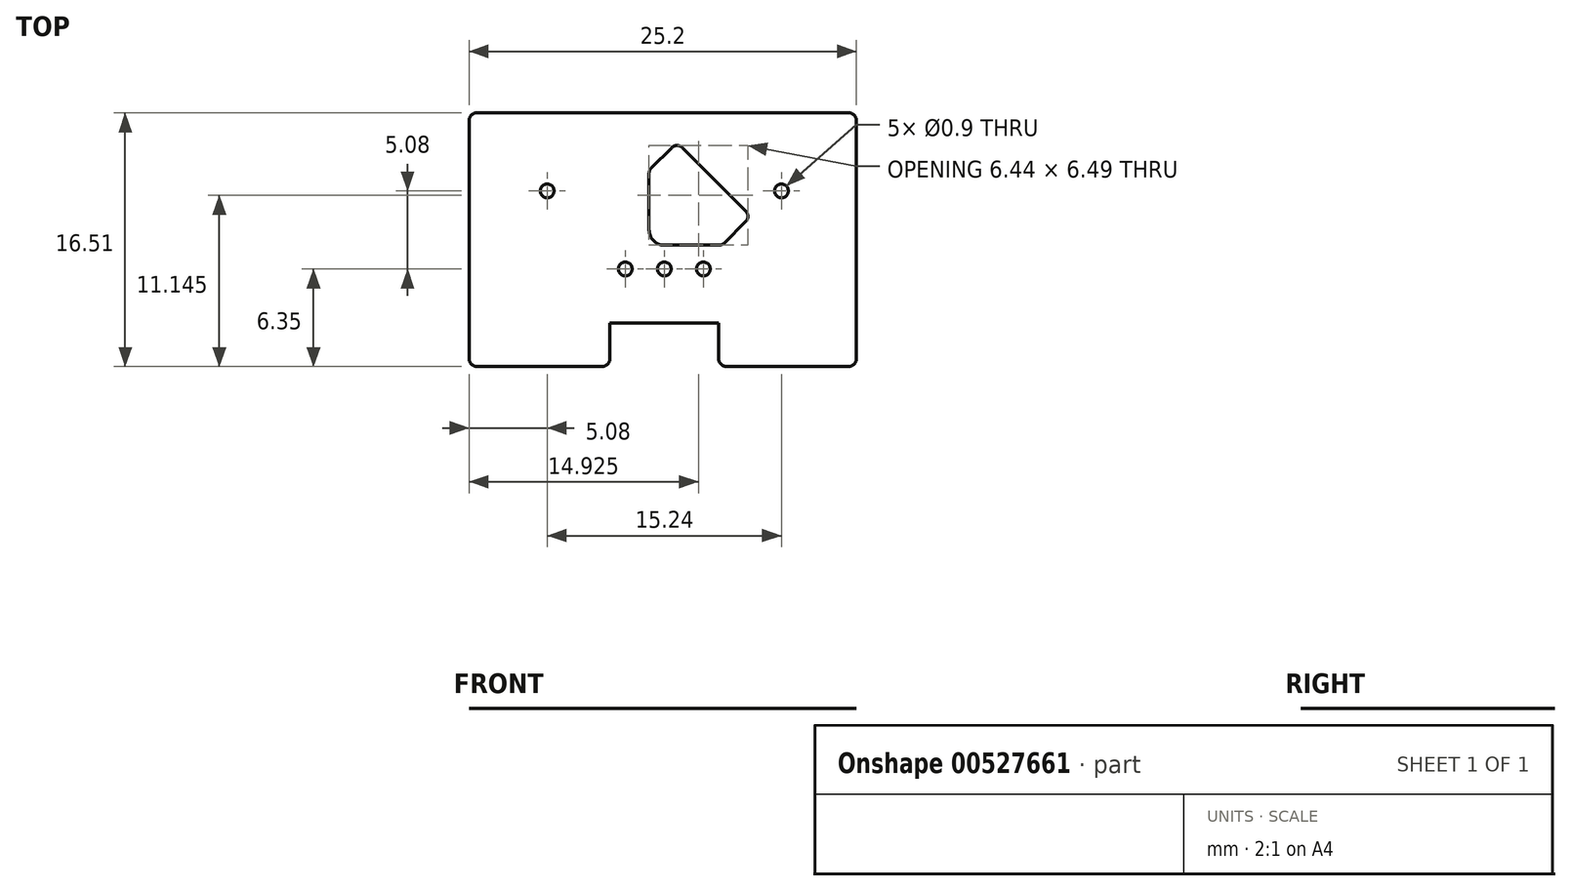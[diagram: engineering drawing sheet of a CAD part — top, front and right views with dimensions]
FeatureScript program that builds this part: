
annotation { "Feature Type Name" : "Feature", "Feature Type Description" : "" }
export const myFeature = defineFeature(function(context is Context, id is Id, definition is map)
    precondition{}
    {
        {
            var Q0;
            Q0=qCreatedBy(makeId("Top.planeOp"),FACE);
            var sketch = newSketch(context, id + "F0", { "sketchPlane" : qUnion([Q0])});
            skCircle(sketch, "E0", {"center": v(0, 0) * mm, "radius": 1 * mm});
            skPoint(sketch, "E1.0.1.0", {"position": v(0, 2.54) * mm});
            skCircle(sketch, "E1.0.1.1", {"center": v(0, 2.54) * mm, "radius": 1 * mm});
            skPoint(sketch, "E1.0.2.0", {"position": v(0, 5.08) * mm});
            skCircle(sketch, "E1.0.2.1", {"center": v(0, 5.08) * mm, "radius": 1 * mm});
            skPoint(sketch, "E1.0.3.0", {"position": v(0, 7.62) * mm});
            skCircle(sketch, "E1.0.3.1", {"center": v(0, 7.62) * mm, "radius": 1 * mm});
            skPoint(sketch, "E1.0.4.0", {"position": v(0, 10.16) * mm});
            skCircle(sketch, "E1.0.4.1", {"center": v(0, 10.16) * mm, "radius": 1 * mm});
            skPoint(sketch, "E1.0.5.0", {"position": v(0, 12.7) * mm});
            skCircle(sketch, "E1.0.5.1", {"center": v(0, 12.7) * mm, "radius": 1 * mm});
            skPoint(sketch, "E1.1.0.0", {"position": v(2.54, 0) * mm});
            skCircle(sketch, "E1.1.0.1", {"center": v(2.54, 0) * mm, "radius": 1 * mm});
            skPoint(sketch, "E1.1.1.0", {"position": v(2.54, 2.54) * mm});
            skCircle(sketch, "E1.1.1.1", {"center": v(2.54, 2.54) * mm, "radius": 1 * mm});
            skPoint(sketch, "E1.1.2.0", {"position": v(2.54, 5.08) * mm});
            skCircle(sketch, "E1.1.2.1", {"center": v(2.54, 5.08) * mm, "radius": 1 * mm});
            skPoint(sketch, "E1.1.3.0", {"position": v(2.54, 7.62) * mm});
            skCircle(sketch, "E1.1.3.1", {"center": v(2.54, 7.62) * mm, "radius": 1 * mm});
            skPoint(sketch, "E1.1.4.0", {"position": v(2.54, 10.16) * mm});
            skCircle(sketch, "E1.1.4.1", {"center": v(2.54, 10.16) * mm, "radius": 1 * mm});
            skPoint(sketch, "E1.1.5.0", {"position": v(2.54, 12.7) * mm});
            skCircle(sketch, "E1.1.5.1", {"center": v(2.54, 12.7) * mm, "radius": 1 * mm});
            skPoint(sketch, "E1.2.0.0", {"position": v(5.08, 0) * mm});
            skCircle(sketch, "E1.2.0.1", {"center": v(5.08, 0) * mm, "radius": 1 * mm});
            skPoint(sketch, "E1.2.1.0", {"position": v(5.08, 2.54) * mm});
            skCircle(sketch, "E1.2.1.1", {"center": v(5.08, 2.54) * mm, "radius": 1 * mm});
            skPoint(sketch, "E1.2.2.0", {"position": v(5.08, 5.08) * mm});
            skCircle(sketch, "E1.2.2.1", {"center": v(5.08, 5.08) * mm, "radius": 1 * mm});
            skPoint(sketch, "E1.2.3.0", {"position": v(5.08, 7.62) * mm});
            skCircle(sketch, "E1.2.3.1", {"center": v(5.08, 7.62) * mm, "radius": 1 * mm});
            skPoint(sketch, "E1.2.4.0", {"position": v(5.08, 10.16) * mm});
            skCircle(sketch, "E1.2.4.1", {"center": v(5.08, 10.16) * mm, "radius": 1 * mm});
            skPoint(sketch, "E1.2.5.0", {"position": v(5.08, 12.7) * mm});
            skCircle(sketch, "E1.2.5.1", {"center": v(5.08, 12.7) * mm, "radius": 1 * mm});
            skPoint(sketch, "E1.3.0.0", {"position": v(7.62, 0) * mm});
            skCircle(sketch, "E1.3.0.1", {"center": v(7.62, 0) * mm, "radius": 1 * mm});
            skPoint(sketch, "E1.3.1.0", {"position": v(7.62, 2.54) * mm});
            skCircle(sketch, "E1.3.1.1", {"center": v(7.62, 2.54) * mm, "radius": 1 * mm});
            skPoint(sketch, "E1.3.2.0", {"position": v(7.62, 5.08) * mm});
            skCircle(sketch, "E1.3.2.1", {"center": v(7.62, 5.08) * mm, "radius": 1 * mm});
            skPoint(sketch, "E1.3.3.0", {"position": v(7.62, 7.62) * mm});
            skCircle(sketch, "E1.3.3.1", {"center": v(7.62, 7.62) * mm, "radius": 1 * mm});
            skPoint(sketch, "E1.3.4.0", {"position": v(7.62, 10.16) * mm});
            skCircle(sketch, "E1.3.4.1", {"center": v(7.62, 10.16) * mm, "radius": 1 * mm});
            skPoint(sketch, "E1.3.5.0", {"position": v(7.62, 12.7) * mm});
            skCircle(sketch, "E1.3.5.1", {"center": v(7.62, 12.7) * mm, "radius": 1 * mm});
            skPoint(sketch, "E1.4.0.0", {"position": v(10.16, 0) * mm});
            skCircle(sketch, "E1.4.0.1", {"center": v(10.16, 0) * mm, "radius": 1 * mm});
            skPoint(sketch, "E1.4.1.0", {"position": v(10.16, 2.54) * mm});
            skCircle(sketch, "E1.4.1.1", {"center": v(10.16, 2.54) * mm, "radius": 1 * mm});
            skPoint(sketch, "E1.4.2.0", {"position": v(10.16, 5.08) * mm});
            skCircle(sketch, "E1.4.2.1", {"center": v(10.16, 5.08) * mm, "radius": 1 * mm});
            skPoint(sketch, "E1.4.3.0", {"position": v(10.16, 7.62) * mm});
            skCircle(sketch, "E1.4.3.1", {"center": v(10.16, 7.62) * mm, "radius": 1 * mm});
            skPoint(sketch, "E1.4.4.0", {"position": v(10.16, 10.16) * mm});
            skCircle(sketch, "E1.4.4.1", {"center": v(10.16, 10.16) * mm, "radius": 1 * mm});
            skPoint(sketch, "E1.4.5.0", {"position": v(10.16, 12.7) * mm});
            skCircle(sketch, "E1.4.5.1", {"center": v(10.16, 12.7) * mm, "radius": 1 * mm});
            skPoint(sketch, "E1.5.0.0", {"position": v(12.7, 0) * mm});
            skCircle(sketch, "E1.5.0.1", {"center": v(12.7, 0) * mm, "radius": 1 * mm});
            skPoint(sketch, "E1.5.1.0", {"position": v(12.7, 2.54) * mm});
            skCircle(sketch, "E1.5.1.1", {"center": v(12.7, 2.54) * mm, "radius": 1 * mm});
            skPoint(sketch, "E1.5.2.0", {"position": v(12.7, 5.08) * mm});
            skCircle(sketch, "E1.5.2.1", {"center": v(12.7, 5.08) * mm, "radius": 1 * mm});
            skPoint(sketch, "E1.5.3.0", {"position": v(12.7, 7.62) * mm});
            skCircle(sketch, "E1.5.3.1", {"center": v(12.7, 7.62) * mm, "radius": 1 * mm});
            skPoint(sketch, "E1.5.4.0", {"position": v(12.7, 10.16) * mm});
            skCircle(sketch, "E1.5.4.1", {"center": v(12.7, 10.16) * mm, "radius": 1 * mm});
            skPoint(sketch, "E1.5.5.0", {"position": v(12.7, 12.7) * mm});
            skCircle(sketch, "E1.5.5.1", {"center": v(12.7, 12.7) * mm, "radius": 1 * mm});
            skPoint(sketch, "E1.6.0.0", {"position": v(15.24, 0) * mm});
            skCircle(sketch, "E1.6.0.1", {"center": v(15.24, 0) * mm, "radius": 1 * mm});
            skPoint(sketch, "E1.6.1.0", {"position": v(15.24, 2.54) * mm});
            skCircle(sketch, "E1.6.1.1", {"center": v(15.24, 2.54) * mm, "radius": 1 * mm});
            skPoint(sketch, "E1.6.2.0", {"position": v(15.24, 5.08) * mm});
            skCircle(sketch, "E1.6.2.1", {"center": v(15.24, 5.08) * mm, "radius": 1 * mm});
            skPoint(sketch, "E1.6.3.0", {"position": v(15.24, 7.62) * mm});
            skCircle(sketch, "E1.6.3.1", {"center": v(15.24, 7.62) * mm, "radius": 1 * mm});
            skPoint(sketch, "E1.6.4.0", {"position": v(15.24, 10.16) * mm});
            skCircle(sketch, "E1.6.4.1", {"center": v(15.24, 10.16) * mm, "radius": 1 * mm});
            skPoint(sketch, "E1.6.5.0", {"position": v(15.24, 12.7) * mm});
            skCircle(sketch, "E1.6.5.1", {"center": v(15.24, 12.7) * mm, "radius": 1 * mm});
            skPoint(sketch, "E1.7.0.0", {"position": v(17.78, 0) * mm});
            skCircle(sketch, "E1.7.0.1", {"center": v(17.78, 0) * mm, "radius": 1 * mm});
            skPoint(sketch, "E1.7.1.0", {"position": v(17.78, 2.54) * mm});
            skCircle(sketch, "E1.7.1.1", {"center": v(17.78, 2.54) * mm, "radius": 1 * mm});
            skPoint(sketch, "E1.7.2.0", {"position": v(17.78, 5.08) * mm});
            skCircle(sketch, "E1.7.2.1", {"center": v(17.78, 5.08) * mm, "radius": 1 * mm});
            skPoint(sketch, "E1.7.3.0", {"position": v(17.78, 7.62) * mm});
            skCircle(sketch, "E1.7.3.1", {"center": v(17.78, 7.62) * mm, "radius": 1 * mm});
            skPoint(sketch, "E1.7.4.0", {"position": v(17.78, 10.16) * mm});
            skCircle(sketch, "E1.7.4.1", {"center": v(17.78, 10.16) * mm, "radius": 1 * mm});
            skPoint(sketch, "E1.7.5.0", {"position": v(17.78, 12.7) * mm});
            skCircle(sketch, "E1.7.5.1", {"center": v(17.78, 12.7) * mm, "radius": 1 * mm});
            skLineSegment(sketch, "E1.direction1", {"start": v(0, 0) * mm, "end": v(2.54, 0) * mm, "construction": true});
            skLineSegment(sketch, "E1.direction2", {"start": v(0, 0) * mm, "end": v(0, 2.54) * mm, "construction": true});
            skPoint(sketch, "E2.0.0.6", {"position": v(0, 15.24) * mm});
            skCircle(sketch, "E2.1.0.6", {"center": v(0, 15.24) * mm, "radius": 1 * mm});
            skPoint(sketch, "E2.0.0.7", {"position": v(0, 17.78) * mm});
            skCircle(sketch, "E2.1.0.7", {"center": v(0, 17.78) * mm, "radius": 1 * mm});
            skPoint(sketch, "E2.0.1.6", {"position": v(2.54, 15.24) * mm});
            skCircle(sketch, "E2.1.1.6", {"center": v(2.54, 15.24) * mm, "radius": 1 * mm});
            skPoint(sketch, "E2.0.1.7", {"position": v(2.54, 17.78) * mm});
            skCircle(sketch, "E2.1.1.7", {"center": v(2.54, 17.78) * mm, "radius": 1 * mm});
            skPoint(sketch, "E2.0.2.6", {"position": v(5.08, 15.24) * mm});
            skCircle(sketch, "E2.1.2.6", {"center": v(5.08, 15.24) * mm, "radius": 1 * mm});
            skPoint(sketch, "E2.0.2.7", {"position": v(5.08, 17.78) * mm});
            skCircle(sketch, "E2.1.2.7", {"center": v(5.08, 17.78) * mm, "radius": 1 * mm});
            skPoint(sketch, "E2.0.3.6", {"position": v(7.62, 15.24) * mm});
            skCircle(sketch, "E2.1.3.6", {"center": v(7.62, 15.24) * mm, "radius": 1 * mm});
            skPoint(sketch, "E2.0.3.7", {"position": v(7.62, 17.78) * mm});
            skCircle(sketch, "E2.1.3.7", {"center": v(7.62, 17.78) * mm, "radius": 1 * mm});
            skPoint(sketch, "E2.0.4.6", {"position": v(10.16, 15.24) * mm});
            skCircle(sketch, "E2.1.4.6", {"center": v(10.16, 15.24) * mm, "radius": 1 * mm});
            skPoint(sketch, "E2.0.4.7", {"position": v(10.16, 17.78) * mm});
            skCircle(sketch, "E2.1.4.7", {"center": v(10.16, 17.78) * mm, "radius": 1 * mm});
            skPoint(sketch, "E2.0.5.6", {"position": v(12.7, 15.24) * mm});
            skCircle(sketch, "E2.1.5.6", {"center": v(12.7, 15.24) * mm, "radius": 1 * mm});
            skPoint(sketch, "E2.0.5.7", {"position": v(12.7, 17.78) * mm});
            skCircle(sketch, "E2.1.5.7", {"center": v(12.7, 17.78) * mm, "radius": 1 * mm});
            skPoint(sketch, "E2.0.6.6", {"position": v(15.24, 15.24) * mm});
            skCircle(sketch, "E2.1.6.6", {"center": v(15.24, 15.24) * mm, "radius": 1 * mm});
            skPoint(sketch, "E2.0.6.7", {"position": v(15.24, 17.78) * mm});
            skCircle(sketch, "E2.1.6.7", {"center": v(15.24, 17.78) * mm, "radius": 1 * mm});
            skPoint(sketch, "E2.0.7.6", {"position": v(17.78, 15.24) * mm});
            skCircle(sketch, "E2.1.7.6", {"center": v(17.78, 15.24) * mm, "radius": 1 * mm});
            skPoint(sketch, "E2.0.7.7", {"position": v(17.78, 17.78) * mm});
            skCircle(sketch, "E2.1.7.7", {"center": v(17.78, 17.78) * mm, "radius": 1 * mm});
            skPoint(sketch, "E3.0.8.0", {"position": v(20.32, 0) * mm});
            skCircle(sketch, "E3.1.8.0", {"center": v(20.32, 0) * mm, "radius": 1 * mm});
            skPoint(sketch, "E3.0.8.1", {"position": v(20.32, 2.54) * mm});
            skCircle(sketch, "E3.1.8.1", {"center": v(20.32, 2.54) * mm, "radius": 1 * mm});
            skPoint(sketch, "E3.0.8.2", {"position": v(20.32, 5.08) * mm});
            skCircle(sketch, "E3.1.8.2", {"center": v(20.32, 5.08) * mm, "radius": 1 * mm});
            skPoint(sketch, "E3.0.8.3", {"position": v(20.32, 7.62) * mm});
            skCircle(sketch, "E3.1.8.3", {"center": v(20.32, 7.62) * mm, "radius": 1 * mm});
            skPoint(sketch, "E3.0.8.4", {"position": v(20.32, 10.16) * mm});
            skCircle(sketch, "E3.1.8.4", {"center": v(20.32, 10.16) * mm, "radius": 1 * mm});
            skPoint(sketch, "E3.0.8.5", {"position": v(20.32, 12.7) * mm});
            skCircle(sketch, "E3.1.8.5", {"center": v(20.32, 12.7) * mm, "radius": 1 * mm});
            skPoint(sketch, "E3.0.8.6", {"position": v(20.32, 15.24) * mm});
            skCircle(sketch, "E3.1.8.6", {"center": v(20.32, 15.24) * mm, "radius": 1 * mm});
            skPoint(sketch, "E3.0.8.7", {"position": v(20.32, 17.78) * mm});
            skCircle(sketch, "E3.1.8.7", {"center": v(20.32, 17.78) * mm, "radius": 1 * mm});
            skPoint(sketch, "E3.0.9.0", {"position": v(22.86, 0) * mm});
            skCircle(sketch, "E3.1.9.0", {"center": v(22.86, 0) * mm, "radius": 1 * mm});
            skPoint(sketch, "E3.0.9.1", {"position": v(22.86, 2.54) * mm});
            skCircle(sketch, "E3.1.9.1", {"center": v(22.86, 2.54) * mm, "radius": 1 * mm});
            skPoint(sketch, "E3.0.9.2", {"position": v(22.86, 5.08) * mm});
            skCircle(sketch, "E3.1.9.2", {"center": v(22.86, 5.08) * mm, "radius": 1 * mm});
            skPoint(sketch, "E3.0.9.3", {"position": v(22.86, 7.62) * mm});
            skCircle(sketch, "E3.1.9.3", {"center": v(22.86, 7.62) * mm, "radius": 1 * mm});
            skPoint(sketch, "E3.0.9.4", {"position": v(22.86, 10.16) * mm});
            skCircle(sketch, "E3.1.9.4", {"center": v(22.86, 10.16) * mm, "radius": 1 * mm});
            skPoint(sketch, "E3.0.9.5", {"position": v(22.86, 12.7) * mm});
            skCircle(sketch, "E3.1.9.5", {"center": v(22.86, 12.7) * mm, "radius": 1 * mm});
            skPoint(sketch, "E3.0.9.6", {"position": v(22.86, 15.24) * mm});
            skCircle(sketch, "E3.1.9.6", {"center": v(22.86, 15.24) * mm, "radius": 1 * mm});
            skPoint(sketch, "E3.0.9.7", {"position": v(22.86, 17.78) * mm});
            skCircle(sketch, "E3.1.9.7", {"center": v(22.86, 17.78) * mm, "radius": 1 * mm});
            skPoint(sketch, "E3.0.10.0", {"position": v(25.4, 0) * mm});
            skCircle(sketch, "E3.1.10.0", {"center": v(25.4, 0) * mm, "radius": 1 * mm});
            skPoint(sketch, "E3.0.10.1", {"position": v(25.4, 2.54) * mm});
            skCircle(sketch, "E3.1.10.1", {"center": v(25.4, 2.54) * mm, "radius": 1 * mm});
            skPoint(sketch, "E3.0.10.2", {"position": v(25.4, 5.08) * mm});
            skCircle(sketch, "E3.1.10.2", {"center": v(25.4, 5.08) * mm, "radius": 1 * mm});
            skPoint(sketch, "E3.0.10.3", {"position": v(25.4, 7.62) * mm});
            skCircle(sketch, "E3.1.10.3", {"center": v(25.4, 7.62) * mm, "radius": 1 * mm});
            skPoint(sketch, "E3.0.10.4", {"position": v(25.4, 10.16) * mm});
            skCircle(sketch, "E3.1.10.4", {"center": v(25.4, 10.16) * mm, "radius": 1 * mm});
            skPoint(sketch, "E3.0.10.5", {"position": v(25.4, 12.7) * mm});
            skCircle(sketch, "E3.1.10.5", {"center": v(25.4, 12.7) * mm, "radius": 1 * mm});
            skPoint(sketch, "E3.0.10.6", {"position": v(25.4, 15.24) * mm});
            skCircle(sketch, "E3.1.10.6", {"center": v(25.4, 15.24) * mm, "radius": 1 * mm});
            skPoint(sketch, "E3.0.10.7", {"position": v(25.4, 17.78) * mm});
            skCircle(sketch, "E3.1.10.7", {"center": v(25.4, 17.78) * mm, "radius": 1 * mm});
            skLineSegment(sketch, "E4", {"start": v(10.16, 2.54) * mm, "end": v(10.16, 0) * mm, "construction": true});
            skPoint(sketch, "E5", {"position": v(10.16, 1.27) * mm});
            skSolve(sketch);
        }
        {
            var Q0;
            Q0=qCreatedBy(makeId("Top.planeOp"),FACE);
            var sketch = newSketch(context, id + "F1", { "sketchPlane" : qUnion([Q0])});
            skPoint(sketch, "E6.0", {"position": v(10.16, 7.62) * mm});
            skLineSegment(sketch, "E7.bottom", {"start": v(10.48, 7.94) * mm, "end": v(9.84, 7.94) * mm});
            skLineSegment(sketch, "E7.top", {"start": v(10.48, 7.3) * mm, "end": v(9.84, 7.3) * mm});
            skLineSegment(sketch, "E7.left", {"start": v(10.48, 7.94) * mm, "end": v(10.48, 7.3) * mm});
            skLineSegment(sketch, "E7.right", {"start": v(9.84, 7.94) * mm, "end": v(9.84, 7.3) * mm});
            skLineSegment(sketch, "E8.bottom", {"start": v(5.4, 13.02) * mm, "end": v(4.76, 13.02) * mm});
            skLineSegment(sketch, "E8.top", {"start": v(5.4, 12.38) * mm, "end": v(4.76, 12.38) * mm});
            skLineSegment(sketch, "E8.left", {"start": v(5.4, 13.02) * mm, "end": v(5.4, 12.38) * mm});
            skLineSegment(sketch, "E8.right", {"start": v(4.76, 13.02) * mm, "end": v(4.76, 12.38) * mm});
            skPoint(sketch, "E8.middle", {"position": v(5.08, 12.7) * mm});
            skLineSegment(sketch, "E9.bottom", {"start": v(20.64, 13.02) * mm, "end": v(20, 13.02) * mm});
            skLineSegment(sketch, "E9.top", {"start": v(20.64, 12.38) * mm, "end": v(20, 12.38) * mm});
            skLineSegment(sketch, "E9.left", {"start": v(20.64, 13.02) * mm, "end": v(20.64, 12.38) * mm});
            skLineSegment(sketch, "E9.right", {"start": v(20, 13.02) * mm, "end": v(20, 12.38) * mm});
            skPoint(sketch, "E9.middle", {"position": v(20.32, 12.7) * mm});
            skLineSegment(sketch, "E10.bottom", {"start": v(13.02, 7.94) * mm, "end": v(12.38, 7.94) * mm});
            skLineSegment(sketch, "E10.top", {"start": v(13.02, 7.3) * mm, "end": v(12.38, 7.3) * mm});
            skLineSegment(sketch, "E10.left", {"start": v(13.02, 7.94) * mm, "end": v(13.02, 7.3) * mm});
            skLineSegment(sketch, "E10.right", {"start": v(12.38, 7.94) * mm, "end": v(12.38, 7.3) * mm});
            skPoint(sketch, "E10.middle", {"position": v(12.7, 7.62) * mm});
            skLineSegment(sketch, "E11.bottom", {"start": v(15.56, 7.94) * mm, "end": v(14.92, 7.94) * mm});
            skLineSegment(sketch, "E11.top", {"start": v(15.56, 7.3) * mm, "end": v(14.92, 7.3) * mm});
            skLineSegment(sketch, "E11.left", {"start": v(15.56, 7.94) * mm, "end": v(15.56, 7.3) * mm});
            skLineSegment(sketch, "E11.right", {"start": v(14.92, 7.94) * mm, "end": v(14.92, 7.3) * mm});
            skPoint(sketch, "E11.middle", {"position": v(15.24, 7.62) * mm});
            skCircle(sketch, "E12.0", {"center": v(12.7, 10.16) * mm, "radius": 1 * mm});
            skCircle(sketch, "E13.0", {"center": v(12.7, 12.7) * mm, "radius": 1 * mm});
            skCircle(sketch, "E14.0", {"center": v(15.24, 10.16) * mm, "radius": 1 * mm});
            skCircle(sketch, "E15.0", {"center": v(10.16, 5.08) * mm, "radius": 1 * mm});
            skCircle(sketch, "E16.0", {"center": v(12.7, 5.08) * mm, "radius": 1 * mm});
            skCircle(sketch, "E17.0", {"center": v(15.24, 5.08) * mm, "radius": 1 * mm});
            skCircle(sketch, "E18.0", {"center": v(10.16, 2.54) * mm, "radius": 1 * mm});
            skCircle(sketch, "E19.0", {"center": v(12.7, 2.54) * mm, "radius": 1 * mm});
            skCircle(sketch, "E20.0", {"center": v(15.24, 2.54) * mm, "radius": 1 * mm});
            skLineSegment(sketch, "E21", {"start": v(9.17, 5.08) * mm, "end": v(9.17, 2.54) * mm});
            skLineSegment(sketch, "E22", {"start": v(11.15, 5.08) * mm, "end": v(11.15, 2.54) * mm});
            skLineSegment(sketch, "E23", {"start": v(11.7, 2.54) * mm, "end": v(11.7, 5.08) * mm});
            skLineSegment(sketch, "E24", {"start": v(13.7, 5.08) * mm, "end": v(13.7, 2.54) * mm});
            skLineSegment(sketch, "E25", {"start": v(14.25, 2.54) * mm, "end": v(14.25, 5.08) * mm});
            skLineSegment(sketch, "E26", {"start": v(16.23, 2.54) * mm, "end": v(16.23, 5.08) * mm});
            skSolve(sketch);
        }
        {
            var Q0;
            Q0=qCreatedBy(makeId("Top.planeOp"),FACE);
            var sketch = newSketch(context, id + "F2", { "sketchPlane" : qUnion([Q0])});
            skLineSegment(sketch, "E27", {"start": v(9.17, 4.09) * mm, "end": v(16.23, 4.09) * mm});
            skLineSegment(sketch, "E28", {"start": v(12.7, 9.17) * mm, "end": v(16.47, 9.17) * mm});
            skLineSegment(sketch, "E29", {"start": v(11.7, 14.05) * mm, "end": v(11.7, 10.16) * mm});
            skArc(sketch, "E30", {"start": v(11.7, 10.16) * mm, "mid": v(12, 9.46) * mm, "end": v(12.7, 9.17) * mm});
            skLineSegment(sketch, "E31.bottom", {"start": v(0, 17.78) * mm, "end": v(25.2, 17.78) * mm});
            skLineSegment(sketch, "E31.top", {"start": v(0, 1.27) * mm, "end": v(9.17, 1.27) * mm});
            skLineSegment(sketch, "E31.left", {"start": v(0, 17.78) * mm, "end": v(0, 1.27) * mm});
            skLineSegment(sketch, "E31.right", {"start": v(25.2, 17.78) * mm, "end": v(25.2, 1.27) * mm});
            skLineSegment(sketch, "E32", {"start": v(9.17, 4.09) * mm, "end": v(9.17, 1.27) * mm});
            skLineSegment(sketch, "E33", {"start": v(16.23, 4.09) * mm, "end": v(16.23, 1.27) * mm});
            skLineSegment(sketch, "E34.trimOffspring", {"start": v(16.23, 1.27) * mm, "end": v(25.2, 1.27) * mm});
            skCircle(sketch, "E35", {"center": v(10.16, 7.62) * mm, "radius": 0.45 * mm});
            skCircle(sketch, "E36", {"center": v(12.7, 7.62) * mm, "radius": 0.45 * mm});
            skCircle(sketch, "E37", {"center": v(15.24, 7.62) * mm, "radius": 0.45 * mm});
            skCircle(sketch, "E38", {"center": v(20.32, 12.7) * mm, "radius": 0.45 * mm});
            skCircle(sketch, "E39", {"center": v(5.08, 12.7) * mm, "radius": 0.45 * mm});
            skLineSegment(sketch, "E40", {"start": v(11.7, 14.05) * mm, "end": v(13.53, 15.87) * mm});
            skLineSegment(sketch, "E41", {"start": v(13.53, 15.87) * mm, "end": v(18.35, 11.05) * mm});
            skLineSegment(sketch, "E42", {"start": v(18.35, 11.05) * mm, "end": v(16.47, 9.17) * mm});
            skSolve(sketch);
        }
        {
            var Q0;
            Q0=makeQuery(id+"F2.imprint","IMPRINT",FACE,{"disambiguationData":[TD([[makeQuery(id+"F2.imprint","IMPRINT",EDGE,{"derivedFrom":sQuery(id+"F2.wireOp",EDGE,"E27")}),1.0]])]});
            extrude(context, id + "F3", {"entities" : qUnion([Q0]), "depth" : 1 / 406.4 * mm, "offsetDistance" : 25.4 * mm});
        }
        {
            var Q0;
            Q0=makeQuery(id+"F3.opExtrude","SWEPT_EDGE",EDGE,{"disambiguationData":[OSD([sQuery(id+"F2.wireOp",EDGE,"E31.right"),sQuery(id+"F2.wireOp",EDGE,"E34.trimOffspring")])]});
            var Q1;
            Q1=makeQuery(id+"F3.opExtrude","SWEPT_EDGE",EDGE,{"disambiguationData":[OSD([sQuery(id+"F2.wireOp",EDGE,"E33"),sQuery(id+"F2.wireOp",EDGE,"E34.trimOffspring")])]});
            var Q2;
            Q2=makeQuery(id+"F3.opExtrude","SWEPT_EDGE",EDGE,{"disambiguationData":[OSD([sQuery(id+"F2.wireOp",EDGE,"E31.top"),sQuery(id+"F2.wireOp",EDGE,"E32")])]});
            var Q3;
            Q3=makeQuery(id+"F3.opExtrude","SWEPT_EDGE",EDGE,{"disambiguationData":[OSD([sQuery(id+"F2.wireOp",EDGE,"E31.top"),sQuery(id+"F2.wireOp",EDGE,"E31.left")])]});
            var Q4;
            Q4=makeQuery(id+"F3.opExtrude","SWEPT_EDGE",EDGE,{"disambiguationData":[OSD([sQuery(id+"F2.wireOp",EDGE,"E31.bottom"),sQuery(id+"F2.wireOp",EDGE,"E31.left")])]});
            var Q5;
            Q5=makeQuery(id+"F3.opExtrude","SWEPT_EDGE",EDGE,{"disambiguationData":[OSD([sQuery(id+"F2.wireOp",EDGE,"E31.bottom"),sQuery(id+"F2.wireOp",EDGE,"E31.right")])]});
            var Q6;
            Q6=makeQuery(id+"F3.opExtrude","SWEPT_EDGE",EDGE,{"disambiguationData":[OSD([sQuery(id+"F2.wireOp",EDGE,"E29"),sQuery(id+"F2.wireOp",EDGE,"E40")])]});
            var Q7;
            Q7=makeQuery(id+"F3.opExtrude","SWEPT_EDGE",EDGE,{"disambiguationData":[OSD([sQuery(id+"F2.wireOp",EDGE,"E40"),sQuery(id+"F2.wireOp",EDGE,"E41")])]});
            var Q8;
            Q8=makeQuery(id+"F3.opExtrude","SWEPT_EDGE",EDGE,{"disambiguationData":[OSD([sQuery(id+"F2.wireOp",EDGE,"E41"),sQuery(id+"F2.wireOp",EDGE,"E42")])]});
            var Q9;
            Q9=makeQuery(id+"F3.opExtrude","SWEPT_EDGE",EDGE,{"disambiguationData":[OSD([sQuery(id+"F2.wireOp",EDGE,"E28"),sQuery(id+"F2.wireOp",EDGE,"E42")])]});
            fillet(context, id + "F4", {"entities" : qUnion([Q0, Q1, Q2, Q3, Q4, Q5, Q6, Q7, Q8, Q9]), "radius" : 0.5 * mm, "tangentPropagation" : true, "allowEdgeOverflow" : false});
        }
    });
